# Revit family: NBS_Allermuir_OffcChrs-en-us-Kin_LowBackStool
name_source: partatom
category: Furniture
revit_build: Autodesk Revit 2018 (Build: 20190510_1515(x64)
units: mm (PartAtom-declared; Revit-internal decimal feet)

## family parameters
Always vertical = Yes
Cut with Voids When Loaded = No
Room Calculation Point = No
Shared = No
Work Plane-Based = No

## types (2) — shared parameters
AssetType = Movable
Category = Pr_40_50_12_57:Office chairs
CodePerformance = ANSI/BIFMA X5.1-2017
Color = Off-Black, White, Crayon Gray, Pistachio, Haze Blue, Aubergine, Seattle Green, Red
DurationUnit = year
ExpectedLife = 10
Finish = Off-Black, White, Crayon Gray, Pistachio, Haze Blue, Aubergine, Seattle Green, Red
FrameFinish = Off black, white, crayon gray, pistachio, seattle green, aubergine, red, haze blue
FrameMountingMaterial = NBS_Allermuir_Plastic_Black
IfcExportAs = IfcFurnitureType
IfcExportType = STOOL
IsBuiltIn = No
LegConnectorFrameMaterial = NBS_Allermuir_Steel_BlackPowderCoat
ManufacturerName = Allermuir
ManufacturerURL = www.allermuir.com
ModelReference = Kin_LowBackStool
NBSCertification = www.nationalbimlibrary.com/cert/to0yicp4
NBSDescription = Office chairs
NBSReference = 45-35-20/330
NominalHeight = 35 "
NominalLength = 18 "
NominalWidth = 18 "
OmniClassCode = 22-12 52 23
OmniClassTitle = Office Seating
OmniClassVersion = Table 22 2012-05-16
ProductInformation = https://www.allermuir.com
SeatDepth = 17.75"
SeatMaterial = NBS_Allermuir_Plastic_Black
SeatWidth = 16.25"
SeatingHeight = 29 "
Status = UNSET
Style = Stool
SustainabilityPerformance = 99% recyclable
Uniclass2015Code = Pr_40_50_12_57
Uniclass2015Title = Office chairs
Uniclass2015Version = Products v1.15
Version = 1
WarrantyDescription = Allermuir warrant that its manufactured products are free from manufacturing defects - in materials or workmanship - for a period of ten (10) years. , Allermuir will repair, or replace (at Allermuir's sole discretion) with comparable free of charge materials / components, any product / component which fails under normal use in a single shift environment, as a result of a defect in the materials and/ or workmanship
WarrantyDurationParts = 10
WarrantyDurationUnit = year
zero-valued in all types: HighestSeatingHeight, LowestSeatingHeight

## per-type parameters (varying)
| type | BIMObjectName | Description | Features | FrameMaterial | FrameType | Material | ModelNumber | Name | NominalDepth | Size |
| Kin_LowBackStool_KIN502 | NBS_Allermuir_OfficeChairs_Kin_LowBackStool_KIN502-US | Low back stool on 4 leg frame | Plastic shell — color: Off-Black, Tubular steel frame finished in Off-Black powder coat, Footrest protector, Plastic glides, Counter height option available, Plastic glides with felt | NBS_Allermuir_Steel_BlackPowderCoat | NBS_Allermuir_OffcChrs_Kin_LowBackStool_4LegFrame : 4LegFrame | Polypropylene, Aluminum Casting | KIN502 | OfficeChairs_KIN502_Kin_Allermuir | 18 " | 18 x 34.75 x 17.50" |
| Kin_LowBackStool_KIN503 | NBS_Allermuir_OfficeChairs_Kin_LowBackStool_KIN503-US | Low back stool on wooden legs | Plastic shell — color: Off-Black, Aluminum leg connector frame finished in Off-Black powder coat, Solid Ash legs with a clear finish, Footrest finished in Off-Black powdercoat, Footrest protector, Plastic glides, Counter height option available, Plastic glides with felt | NBS_Allermuir_Ash_ClearFinish | NBS_Allermuir_OffcChrs_Kin_LowBackStool_WoodLegs : WoodLegs | Polypropylene, Aluminum Casting, Solid Wood | KIN503 | OfficeChairs_KIN503_Kin_Allermuir | 19 " | 19 x 34.75 x 17.5" |

## geometry (parser evidence)
native form markers: Sweep x12
no freeform markers — native parametric forms only
